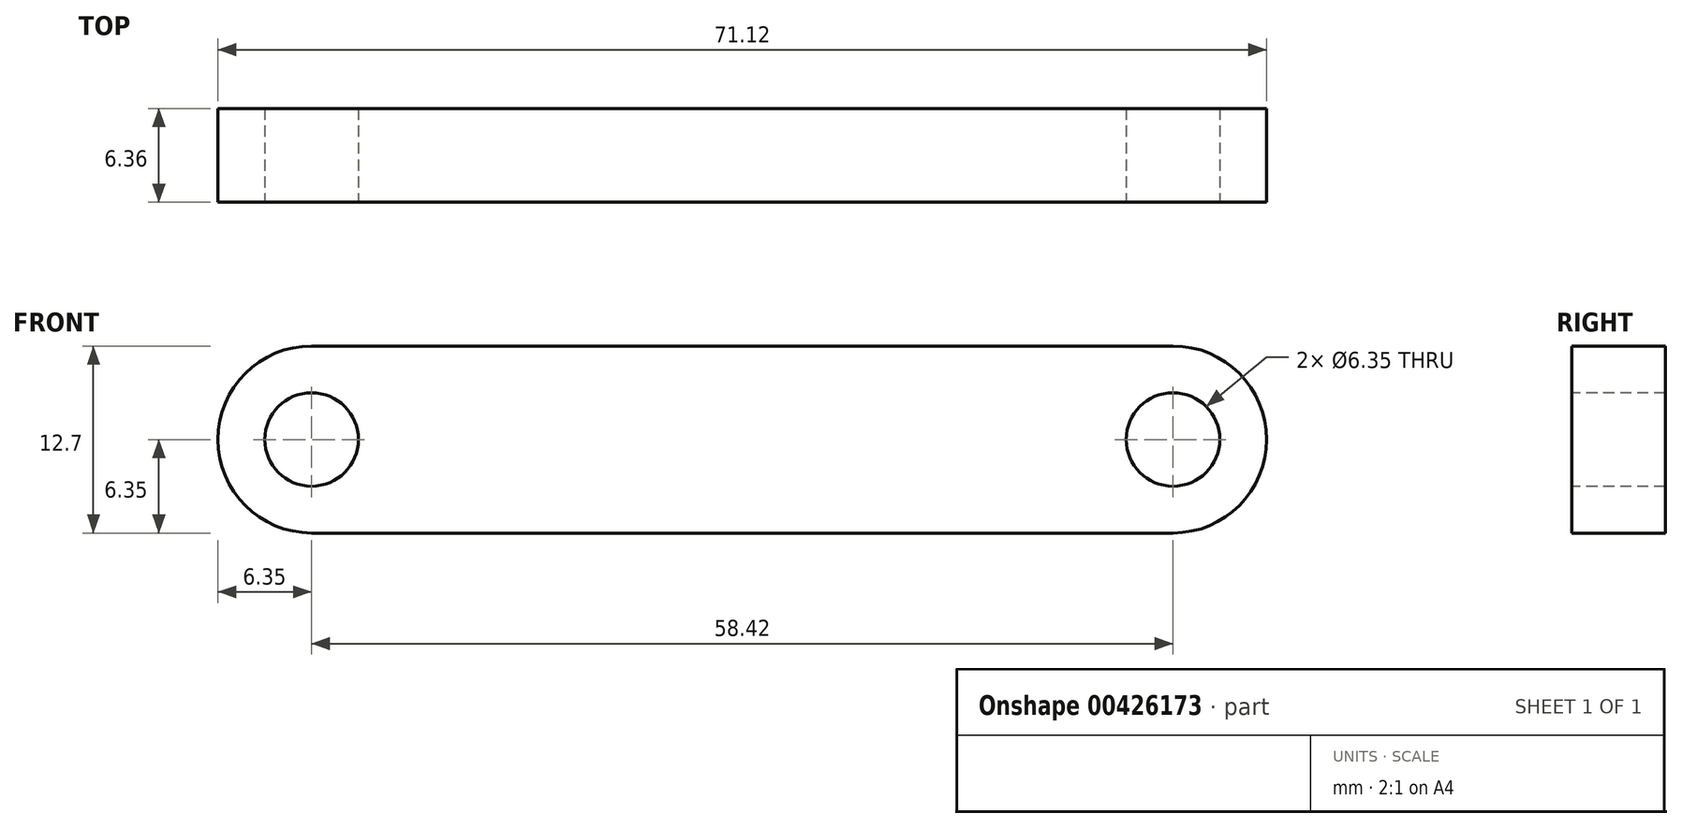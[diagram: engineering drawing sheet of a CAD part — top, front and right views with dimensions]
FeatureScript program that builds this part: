
annotation { "Feature Type Name" : "Feature", "Feature Type Description" : "" }
export const myFeature = defineFeature(function(context is Context, id is Id, definition is map)
    precondition{}
    {
        {
            var Q0;
            Q0=qCreatedBy(makeId("Front.planeOp"),FACE);
            var sketch = newSketch(context, id + "F0", { "sketchPlane" : qUnion([Q0])});
            skLineSegment(sketch, "E0.bottom", {"start": v(-29.21, 6.35) * mm, "end": v(29.21, 6.35) * mm});
            skLineSegment(sketch, "E0.top", {"start": v(-29.21, -6.35) * mm, "end": v(29.21, -6.35) * mm});
            skArc(sketch, "E1", {"start": v(-29.21, 6.35) * mm, "mid": v(-35.56, 0) * mm, "end": v(-29.21, -6.35) * mm});
            skArc(sketch, "E2", {"start": v(29.21, -6.35) * mm, "mid": v(35.56, 0) * mm, "end": v(29.21, 6.35) * mm});
            skSolve(sketch);
        }
        {
            var Q0;
            Q0 = qSketchRegion(id + "F0", true);
            extrude(context, id + "F1", {"entities" : qUnion([Q0]), "endBound" : BoundingType.SYMMETRIC, "depth" : 6.35 * mm});
        }
        {
            var Q0;
            Q0=makeQuery(id+"F1.opExtrude","CAP_FACE",FACE,{"disambiguationData":[OSD([sQuery(id+"F0.wireOp",EDGE,"E0.bottom"),sQuery(id+"F0.wireOp",EDGE,"E0.top"),sQuery(id+"F0.wireOp",EDGE,"E1"),sQuery(id+"F0.wireOp",EDGE,"E2")])],"isStart":false});
            var sketch = newSketch(context, id + "F2", { "sketchPlane" : qUnion([Q0])});
            skCircle(sketch, "E3", {"center": v(29.21, 0) * mm, "radius": 3.18 * mm});
            skCircle(sketch, "E4", {"center": v(-29.21, 0) * mm, "radius": 3.18 * mm});
            skSolve(sketch);
        }
        {
            var Q0;
            Q0 = qSketchRegion(id + "F2", true);
            extrude(context, id + "F3", {"entities" : qUnion([Q0]), "operationType" : NewBodyOperationType.REMOVE, "endBound" : BoundingType.THROUGH_ALL, "oppositeDirection" : true, "depth" : 25.4 * mm});
        }
    });
